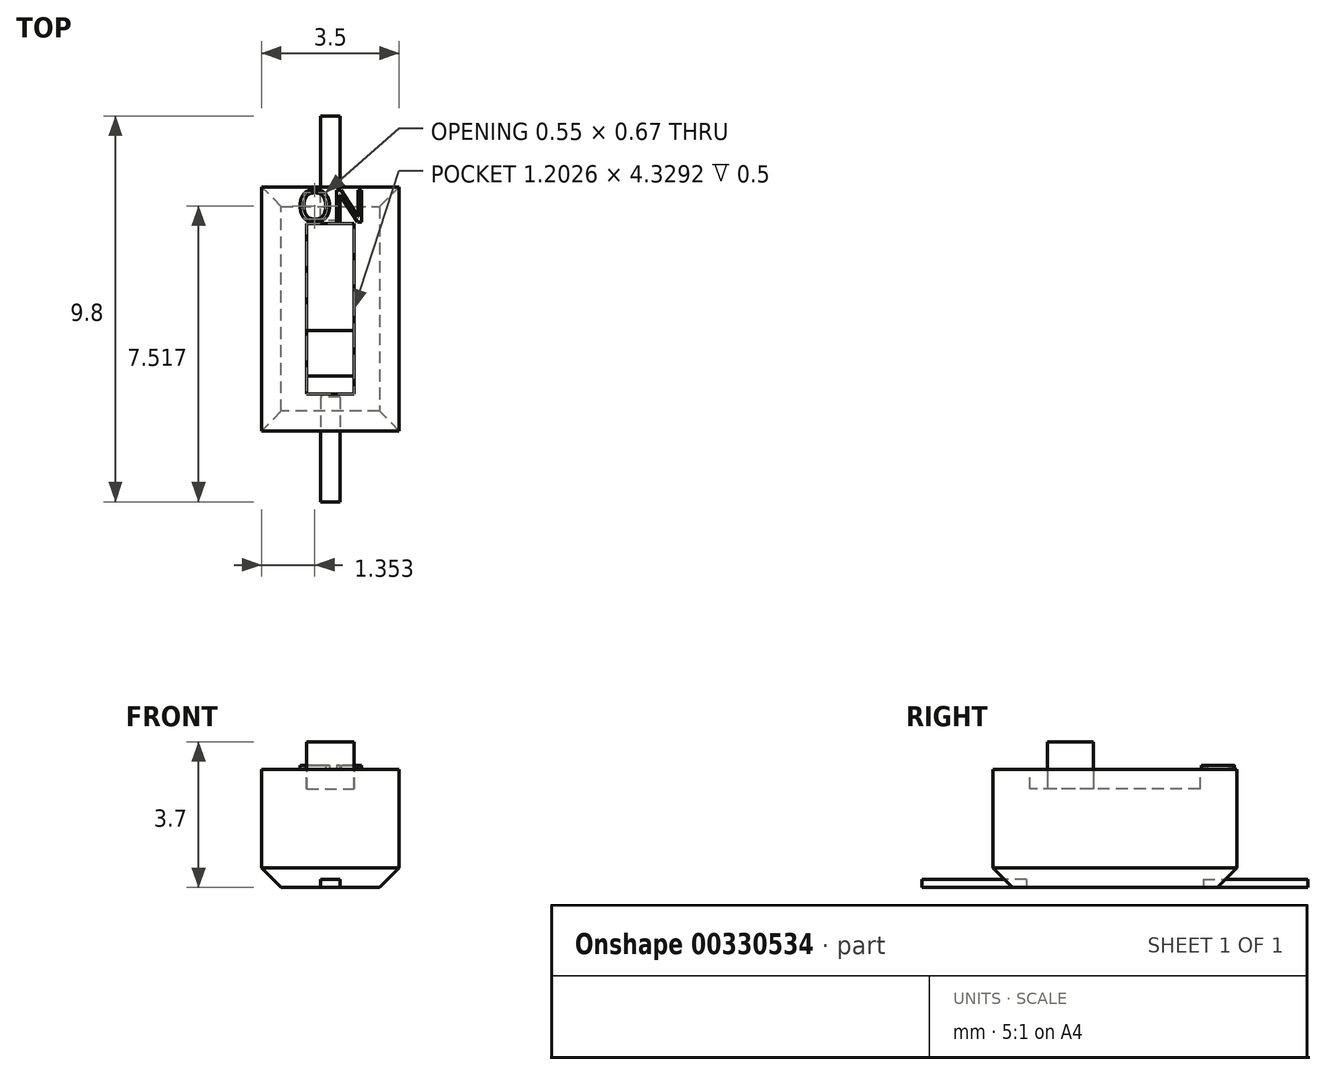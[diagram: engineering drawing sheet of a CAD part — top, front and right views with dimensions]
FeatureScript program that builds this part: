
annotation { "Feature Type Name" : "Feature", "Feature Type Description" : "" }
export const myFeature = defineFeature(function(context is Context, id is Id, definition is map)
    precondition{}
    {
        {
            var Q0;
            Q0=qCreatedBy(makeId("Top.planeOp"),FACE);
            var sketch = newSketch(context, id + "F0", { "sketchPlane" : qUnion([Q0])});
            skLineSegment(sketch, "E0.bottom", {"start": v(1.75, -3.1) * mm, "end": v(-1.75, -3.1) * mm});
            skLineSegment(sketch, "E0.top", {"start": v(1.75, 3.1) * mm, "end": v(-1.75, 3.1) * mm});
            skLineSegment(sketch, "E0.left", {"start": v(1.75, -3.1) * mm, "end": v(1.75, 3.1) * mm});
            skLineSegment(sketch, "E0.right", {"start": v(-1.75, -3.1) * mm, "end": v(-1.75, 3.1) * mm});
            skPoint(sketch, "E0.middle", {"position": v(0, 0) * mm});
            skSolve(sketch);
        }
        {
            var Q0;
            Q0 = qSketchRegion(id + "F0", true);
            extrude(context, id + "F1", {"entities" : qUnion([Q0]), "depth" : 2.5 * mm, "offsetDistance" : 25 * mm, "hasSecondDirection" : true, "secondDirectionOppositeDirection" : true, "secondDirectionDepth" : .5 * mm});
        }
        {
            var Q0;
            Q0=makeQuery(id+"F1.opExtrude","CAP_EDGE",EDGE,{"disambiguationData":[OSD([sQuery(id+"F0.wireOp",EDGE,"E0.bottom")])],"isStart":true});
            var Q1;
            Q1=makeQuery(id+"F1.opExtrude","CAP_EDGE",EDGE,{"disambiguationData":[OSD([sQuery(id+"F0.wireOp",EDGE,"E0.left")])],"isStart":true});
            var Q2;
            Q2=makeQuery(id+"F1.opExtrude","CAP_EDGE",EDGE,{"disambiguationData":[OSD([sQuery(id+"F0.wireOp",EDGE,"E0.top")])],"isStart":true});
            var Q3;
            Q3=makeQuery(id+"F1.opExtrude","CAP_EDGE",EDGE,{"disambiguationData":[OSD([sQuery(id+"F0.wireOp",EDGE,"E0.right")])],"isStart":true});
            chamfer(context, id + "F2", {"entities" : qUnion([Q0, Q1, Q2, Q3]), "width" : .5 * mm, "tangentPropagation" : true});
        }
        {
            var Q0;
            Q0=makeQuery(id+"F1.opExtrude","CAP_FACE",FACE,{"disambiguationData":[OSD([sQuery(id+"F0.wireOp",EDGE,"E0.bottom"),sQuery(id+"F0.wireOp",EDGE,"E0.top"),sQuery(id+"F0.wireOp",EDGE,"E0.left"),sQuery(id+"F0.wireOp",EDGE,"E0.right")])],"isStart":false});
            var sketch = newSketch(context, id + "F3", { "sketchPlane" : qUnion([Q0])});
            skLineSegment(sketch, "E1.bottom", {"start": v(-0.6, 2.16) * mm, "end": v(0.6, 2.16) * mm});
            skLineSegment(sketch, "E1.top", {"start": v(-0.6, -2.16) * mm, "end": v(0.6, -2.16) * mm});
            skLineSegment(sketch, "E1.left", {"start": v(-0.6, 2.16) * mm, "end": v(-0.6, -2.16) * mm});
            skLineSegment(sketch, "E1.right", {"start": v(0.6, 2.16) * mm, "end": v(0.6, -2.16) * mm});
            skPoint(sketch, "E1.middle", {"position": v(0, 0) * mm});
            skSolve(sketch);
        }
        {
            var Q0;
            Q0 = qSketchRegion(id + "F3", true);
            extrude(context, id + "F4", {"entities" : qUnion([Q0]), "operationType" : NewBodyOperationType.REMOVE, "oppositeDirection" : true, "depth" : 0.5 * mm, "offsetDistance" : 25 * mm});
        }
        {
            var Q0;
            Q0=makeQuery(id+"F4.boolean.opBoolean","COPY",FACE,{"derivedFrom":makeQuery(id+"F4.opExtrude","CAP_FACE",FACE,{"disambiguationData":[OSD([sQuery(id+"F3.wireOp",EDGE,"E1.bottom"),sQuery(id+"F3.wireOp",EDGE,"E1.top"),sQuery(id+"F3.wireOp",EDGE,"E1.left"),sQuery(id+"F3.wireOp",EDGE,"E1.right")])],"isStart":false})});
            var sketch = newSketch(context, id + "F5", { "sketchPlane" : qUnion([Q0])});
            skLineSegment(sketch, "E2.bottom", {"start": v(-0.6, -0.55) * mm, "end": v(0.6, -0.55) * mm});
            skLineSegment(sketch, "E2.top", {"start": v(-0.6, -1.7) * mm, "end": v(0.6, -1.7) * mm});
            skLineSegment(sketch, "E2.left", {"start": v(-0.6, -0.55) * mm, "end": v(-0.6, -1.7) * mm});
            skLineSegment(sketch, "E2.right", {"start": v(0.6, -0.55) * mm, "end": v(0.6, -1.7) * mm});
            skPoint(sketch, "E2.middle", {"position": v(0, -1.13) * mm});
            skSolve(sketch);
        }
        {
            var Q0;
            Q0 = qSketchRegion(id + "F5", true);
            extrude(context, id + "F6", {"entities" : qUnion([Q0]), "depth" : 1.2 * mm, "offsetDistance" : 25 * mm});
        }
        {
            var Q0;
            Q0=makeQuery(id+"F1.opExtrude","CAP_FACE",FACE,{"disambiguationData":[OSD([sQuery(id+"F0.wireOp",EDGE,"E0.bottom"),sQuery(id+"F0.wireOp",EDGE,"E0.top"),sQuery(id+"F0.wireOp",EDGE,"E0.left"),sQuery(id+"F0.wireOp",EDGE,"E0.right")])],"isStart":false});
            var sketch = newSketch(context, id + "F7", { "sketchPlane" : qUnion([Q0])});
            skText(sketch, "E3", { "text": "ON", "fontName": "OpenSans-Regular.ttf"});
            const initialGuessF7  = {"E3": [-0.00084, 0.00221, 1, 0, 0.00082]};
            skSetInitialGuess(sketch, initialGuessF7);
            skSolve(sketch);
        }
        {
            var Q0;
            Q0 = qSketchRegion(id + "F7", true);
            extrude(context, id + "F8", {"entities" : qUnion([Q0]), "depth" : .1 * mm, "offsetDistance" : 25 * mm});
        }
        {
            var Q0;
            Q0=makeQuery(id+"F1.opExtrude","CAP_FACE",FACE,{"disambiguationData":[OSD([sQuery(id+"F0.wireOp",EDGE,"E0.bottom"),sQuery(id+"F0.wireOp",EDGE,"E0.top"),sQuery(id+"F0.wireOp",EDGE,"E0.left"),sQuery(id+"F0.wireOp",EDGE,"E0.right")])],"isStart":true});
            var sketch = newSketch(context, id + "F9", { "sketchPlane" : qUnion([Q0])});
            skLineSegment(sketch, "E4", {"start": v(-1.25, 0) * mm, "end": v(1.25, 0) * mm, "construction": true});
            skLineSegment(sketch, "E5.bottom", {"start": v(0.25, -2.24) * mm, "end": v(-0.25, -2.24) * mm});
            skLineSegment(sketch, "E5.top", {"start": v(0.25, -4.9) * mm, "end": v(-0.25, -4.9) * mm});
            skLineSegment(sketch, "E5.left", {"start": v(0.25, -2.24) * mm, "end": v(0.25, -4.9) * mm});
            skLineSegment(sketch, "E5.right", {"start": v(-0.25, -2.24) * mm, "end": v(-0.25, -4.9) * mm});
            skPoint(sketch, "E5.middle", {"position": v(0, -3.57) * mm});
            skPoint(sketch, "E6", {"position": v(0, -2.6) * mm});
            skPoint(sketch, "E7.MirrorP", {"position": v(0, 2.6) * mm});
            skLineSegment(sketch, "E8.MirrorCS", {"start": v(0.25, 2.24) * mm, "end": v(-0.25, 2.24) * mm});
            skPoint(sketch, "E9.MirrorP", {"position": v(0, 3.57) * mm});
            skLineSegment(sketch, "E10.MirrorCS", {"start": v(-0.25, 2.24) * mm, "end": v(-0.25, 4.9) * mm});
            skLineSegment(sketch, "E11.MirrorCS", {"start": v(0.25, 4.9) * mm, "end": v(-0.25, 4.9) * mm});
            skLineSegment(sketch, "E12.MirrorCS", {"start": v(0.25, 2.24) * mm, "end": v(0.25, 4.9) * mm});
            skSolve(sketch);
        }
        {
            var Q0;
            Q0 = qSketchRegion(id + "F9", true);
            extrude(context, id + "F10", {"entities" : qUnion([Q0]), "oppositeDirection" : true, "depth" : .2 * mm, "offsetDistance" : 25 * mm});
        }
    });
